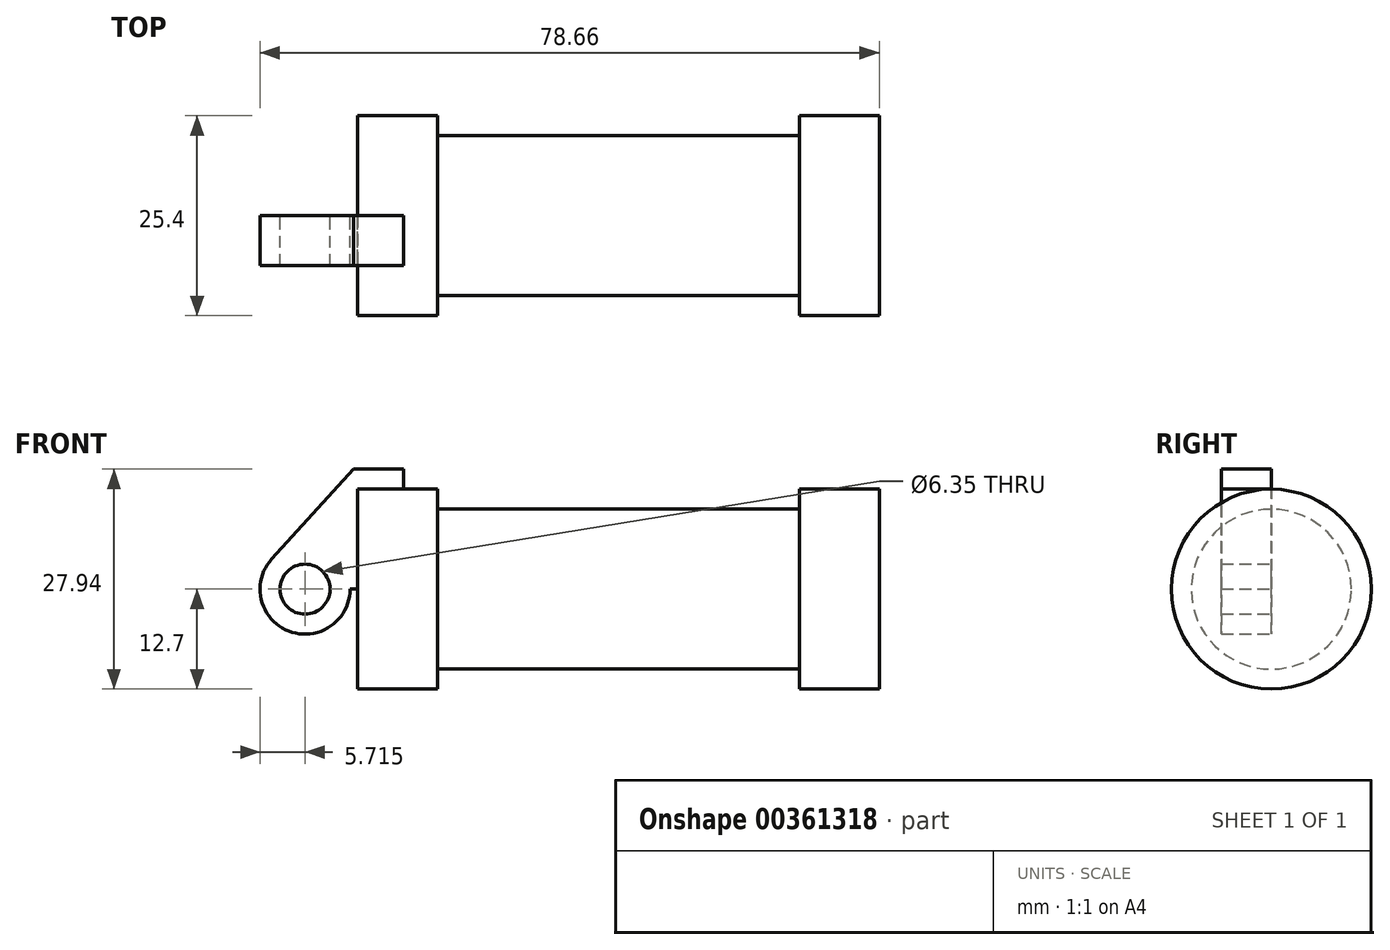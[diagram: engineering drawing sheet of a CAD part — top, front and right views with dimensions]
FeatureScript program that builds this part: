
annotation { "Feature Type Name" : "Feature", "Feature Type Description" : "" }
export const myFeature = defineFeature(function(context is Context, id is Id, definition is map)
    precondition{}
    {
        {
            var Q0;
            Q0=qCreatedBy(makeId("Front.planeOp"),FACE);
            var sketch = newSketch(context, id + "F0", { "sketchPlane" : qUnion([Q0])});
            skLineSegment(sketch, "E0", {"start": v(0, 0) * mm, "end": v(0, 12.7) * mm});
            skLineSegment(sketch, "E1", {"start": v(0, 12.7) * mm, "end": v(10.16, 12.7) * mm});
            skLineSegment(sketch, "E2", {"start": v(10.16, 12.7) * mm, "end": v(10.16, 10.16) * mm});
            skLineSegment(sketch, "E3", {"start": v(10.16, 10.16) * mm, "end": v(56.13, 10.16) * mm});
            skLineSegment(sketch, "E4", {"start": v(56.13, 10.16) * mm, "end": v(56.13, 12.7) * mm});
            skLineSegment(sketch, "E5", {"start": v(56.13, 12.7) * mm, "end": v(66.3, 12.7) * mm});
            skLineSegment(sketch, "E6", {"start": v(66.3, 12.7) * mm, "end": v(66.3, 0) * mm});
            skLineSegment(sketch, "E7", {"start": v(66.3, 0) * mm, "end": v(0, 0) * mm});
            skLineSegment(sketch, "E8", {"start": v(5.84, 15.24) * mm, "end": v(-0.5, 15.24) * mm});
            skLineSegment(sketch, "E9", {"start": v(-0.5, 15.24) * mm, "end": v(-10.88, 3.85) * mm});
            skLineSegment(sketch, "E10", {"start": v(0, 0) * mm, "end": v(-6.65, 0) * mm});
            skCircle(sketch, "E11", {"center": v(-6.65, 0) * mm, "radius": 5.72 * mm});
            skCircle(sketch, "E12", {"center": v(-6.65, 0) * mm, "radius": 3.18 * mm});
            skLineSegment(sketch, "E13", {"start": v(5.84, 15.24) * mm, "end": v(5.84, -9.4) * mm});
            skLineSegment(sketch, "E14", {"start": v(5.84, -9.4) * mm, "end": v(-8.18, -5.5) * mm});
            skSolve(sketch);
        }
        {
            var Q0;
            {var subQ0=sQuery(id+"F0.wireOp",EDGE,"E2");Q0=makeQuery(id+"F0.imprint","IMPRINT",FACE,{"disambiguationData":[TD([[makeQuery(id+"F0.imprint","IMPRINT",EDGE,{"derivedFrom":subQ0}),-1.0]])]});}
            var Q1;
            {var subQ0=sQuery(id+"F0.wireOp",EDGE,"E0");Q1=makeQuery(id+"F0.imprint","IMPRINT",FACE,{"disambiguationData":[TD([[makeQuery(id+"F0.imprint","IMPRINT",EDGE,{"derivedFrom":subQ0}),-1.0]])]});}
            var Q2;
            Q2=sQuery(id+"F0.wireOp",EDGE,"E7");
            revolve(context, id + "F1", {"entities" : qUnion([Q0, Q1]), "axis" : qUnion([Q2]), "revolveType" : RevolveType.FULL});
        }
        {
            var Q0;
            {var subQ1=sQuery(id+"F0.wireOp",EDGE,"E0");Q0=makeQuery(id+"F0.imprint","IMPRINT",FACE,{"disambiguationData":[TD([[makeQuery(id+"F0.imprint","IMPRINT",EDGE,{"derivedFrom":subQ1}),1.0]])]});}
            var Q1;
            {var subQ5=sQuery(id+"F0.wireOp",EDGE,"E12");Q1=makeQuery(id+"F0.imprint","IMPRINT",FACE,{"disambiguationData":[TD([[makeQuery(id+"F0.imprint","IMPRINT",EDGE,{"derivedFrom":subQ5}),-1.0]])]});}
            extrude(context, id + "F2", {"entities" : qUnion([Q0, Q1]), "depth" : 6.35 * mm});
        }
    });
